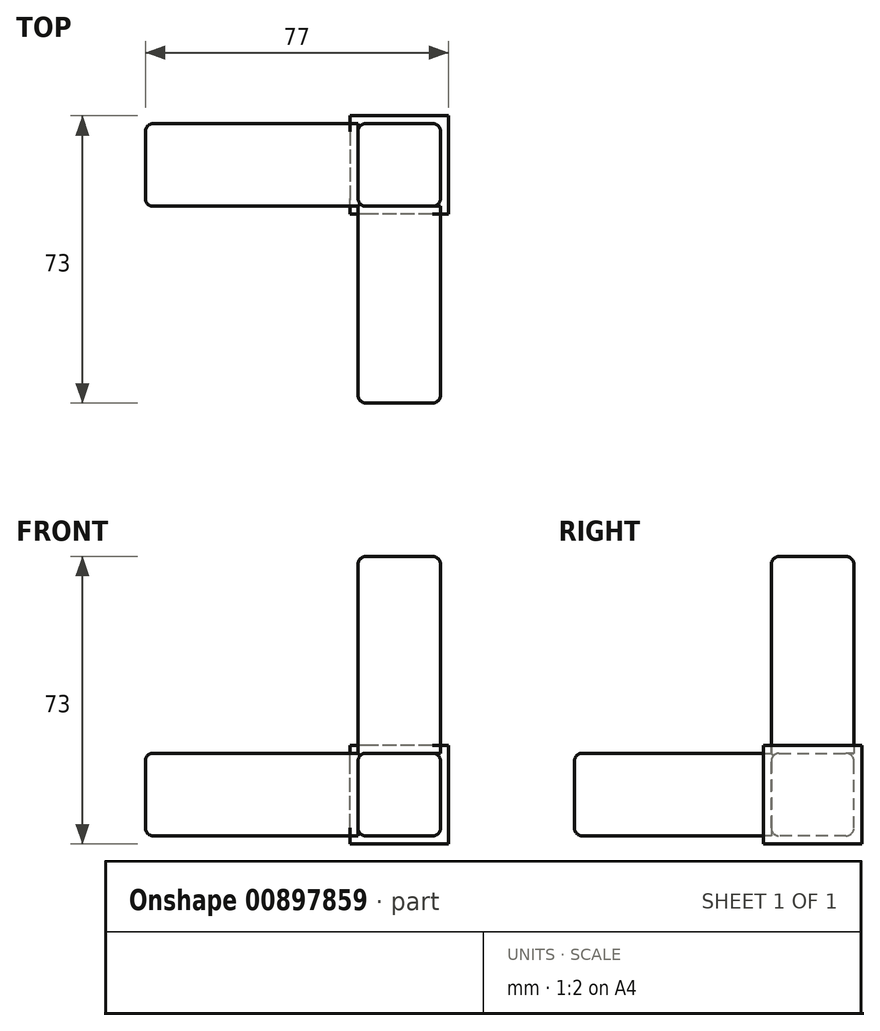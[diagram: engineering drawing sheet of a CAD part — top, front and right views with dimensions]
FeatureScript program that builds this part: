
annotation { "Feature Type Name" : "Feature", "Feature Type Description" : "" }
export const myFeature = defineFeature(function(context is Context, id is Id, definition is map)
    precondition{}
    {
        {
            var Q0;
            Q0=qCreatedBy(makeId("Front.planeOp"),FACE);
            var sketch = newSketch(context, id + "F0", { "sketchPlane" : qUnion([Q0])});
            skLineSegment(sketch, "E0.bottom", {"start": v(37.5, -10.5) * mm, "end": v(-37.5, -10.5) * mm});
            skLineSegment(sketch, "E0.top", {"start": v(16.5, 10.5) * mm, "end": v(-37.5, 10.5) * mm});
            skLineSegment(sketch, "E0.left", {"start": v(37.5, -10.5) * mm, "end": v(37.5, 10.5) * mm});
            skLineSegment(sketch, "E0.right", {"start": v(-37.5, -10.5) * mm, "end": v(-37.5, 10.5) * mm});
            skPoint(sketch, "E0.middle", {"position": v(0, 0) * mm});
            skLineSegment(sketch, "E1", {"start": v(37.5, 10.5) * mm, "end": v(37.5, 60.5) * mm});
            skLineSegment(sketch, "E2", {"start": v(37.5, 60.5) * mm, "end": v(16.5, 60.5) * mm});
            skLineSegment(sketch, "E3", {"start": v(16.5, 60.5) * mm, "end": v(16.5, 10.5) * mm});
            skLineSegment(sketch, "E4", {"start": v(16.5, 10.5) * mm, "end": v(37.5, -10.5) * mm, "construction": true});
            skLineSegment(sketch, "E5", {"start": v(37.5, 10.5) * mm, "end": v(16.5, -10.5) * mm, "construction": true});
            skLineSegment(sketch, "E6.bottom", {"start": v(39.5, -12.5) * mm, "end": v(14.5, -12.5) * mm});
            skLineSegment(sketch, "E6.top", {"start": v(39.5, 12.5) * mm, "end": v(14.5, 12.5) * mm});
            skLineSegment(sketch, "E6.left", {"start": v(39.5, -12.5) * mm, "end": v(39.5, 12.5) * mm});
            skLineSegment(sketch, "E6.right", {"start": v(14.5, -12.5) * mm, "end": v(14.5, 12.5) * mm});
            skPoint(sketch, "E6.middle", {"position": v(27, 0) * mm});
            skSolve(sketch);
        }
        {
            var Q0;
            {var subQ0=sQuery(id+"F0.wireOp",EDGE,"E2");Q0=makeQuery(id+"F0.imprint","IMPRINT",FACE,{"disambiguationData":[TD([[makeQuery(id+"F0.imprint","IMPRINT",EDGE,{"derivedFrom":subQ0}),1.0]])]});}
            var Q1;
            {var subQ0=sQuery(id+"F0.wireOp",EDGE,"E0.right");Q1=makeQuery(id+"F0.imprint","IMPRINT",FACE,{"disambiguationData":[TD([[makeQuery(id+"F0.imprint","IMPRINT",EDGE,{"derivedFrom":subQ0}),-1.0]])]});}
            var Q2;
            {var subQ1=sQuery(id+"F0.wireOp",EDGE,"E0.left");Q2=makeQuery(id+"F0.imprint","IMPRINT",FACE,{"disambiguationData":[TD([[makeQuery(id+"F0.imprint","IMPRINT",EDGE,{"derivedFrom":subQ1}),1.0]])]});}
            extrude(context, id + "F1", {"entities" : qUnion([Q0, Q1, Q2]), "depth" : 21 * mm, "offsetDistance" : 25 * mm});
        }
        {
            var Q0;
            {var subQ1=sQuery(id+"F0.wireOp",EDGE,"E0.left");Q0=makeQuery(id+"F0.imprint","IMPRINT",FACE,{"disambiguationData":[TD([[makeQuery(id+"F0.imprint","IMPRINT",EDGE,{"derivedFrom":subQ1}),-1.0]])]});}
            var Q1;
            {var subQ0=sQuery(id+"F0.wireOp",EDGE,"E3");var subQ1=sQuery(id+"F0.wireOp",EDGE,"E0.top");var subQ2=makeQuery(id+"F0.imprint","INTERSECT",VERTEX,{"derivedFrom":[subQ1,subQ0]});Q1=makeQuery(id+"F0.imprint","IMPRINT",FACE,{"disambiguationData":[TD([[makeQuery(id+"F0.imprint","IMPRINT",EDGE,{"disambiguationData":[TD([[subQ2,-1.0]])],"derivedFrom":subQ1}),-1.0]])]});}
            var Q2;
            {var subQ1=sQuery(id+"F0.wireOp",EDGE,"E0.left");Q2=makeQuery(id+"F0.imprint","IMPRINT",FACE,{"disambiguationData":[TD([[makeQuery(id+"F0.imprint","IMPRINT",EDGE,{"derivedFrom":subQ1}),1.0]])]});}
            extrude(context, id + "F2", {"entities" : qUnion([Q0, Q1, Q2]), "operationType" : NewBodyOperationType.ADD, "oppositeDirection" : true, "depth" : 2 * mm, "offsetDistance" : 25 * mm});
        }
        {
            var Q0;
            Q0=makeQuery(id+"F1.opExtrude","CAP_FACE",FACE,{"disambiguationData":[OSD([sQuery(id+"F0.wireOp",EDGE,"E0.bottom"),sQuery(id+"F0.wireOp",EDGE,"E0.top"),sQuery(id+"F0.wireOp",EDGE,"E0.left"),sQuery(id+"F0.wireOp",EDGE,"E0.right"),sQuery(id+"F0.wireOp",EDGE,"E1"),sQuery(id+"F0.wireOp",EDGE,"E2"),sQuery(id+"F0.wireOp",EDGE,"E3")])],"isStart":false});
            var sketch = newSketch(context, id + "F3", { "sketchPlane" : qUnion([Q0])});
            skPoint(sketch, "E7.0", {"position": v(14.5, 12.5) * mm});
            skPoint(sketch, "E8.0", {"position": v(39.5, 12.5) * mm});
            skPoint(sketch, "E9.0", {"position": v(39.5, -12.5) * mm});
            skPoint(sketch, "E10.0", {"position": v(14.5, -12.5) * mm});
            skLineSegment(sketch, "E11.bottom", {"start": v(14.5, 12.5) * mm, "end": v(39.5, 12.5) * mm, "construction": true});
            skLineSegment(sketch, "E11.top", {"start": v(14.5, -12.5) * mm, "end": v(39.5, -12.5) * mm, "construction": true});
            skLineSegment(sketch, "E11.left", {"start": v(14.5, 12.5) * mm, "end": v(14.5, -12.5) * mm, "construction": true});
            skLineSegment(sketch, "E11.right", {"start": v(39.5, 12.5) * mm, "end": v(39.5, -12.5) * mm});
            skLineSegment(sketch, "E12.bottom", {"start": v(16.5, 10.5) * mm, "end": v(37.5, 10.5) * mm});
            skLineSegment(sketch, "E12.top", {"start": v(16.5, -10.5) * mm, "end": v(37.5, -10.5) * mm});
            skLineSegment(sketch, "E12.left", {"start": v(16.5, 10.5) * mm, "end": v(16.5, -10.5) * mm});
            skLineSegment(sketch, "E12.right", {"start": v(37.5, 10.5) * mm, "end": v(37.5, -10.5) * mm});
            skSolve(sketch);
        }
        {
            var Q0;
            Q0=makeQuery(id+"F1.opExtrude","SWEPT_FACE",FACE,{"disambiguationData":[OSD([sQuery(id+"F0.wireOp",EDGE,"E0.left"),sQuery(id+"F0.wireOp",EDGE,"E1")])]});
            var sketch = newSketch(context, id + "F4", { "sketchPlane" : qUnion([Q0])});
            skPoint(sketch, "E13.0", {"position": v(2, 12.5) * mm});
            skPoint(sketch, "E14.0", {"position": v(2, -12.5) * mm});
            skLineSegment(sketch, "E15", {"start": v(2, 12.5) * mm, "end": v(-23, 12.5) * mm});
            skLineSegment(sketch, "E16", {"start": v(-23, 12.5) * mm, "end": v(-23, -12.5) * mm});
            skLineSegment(sketch, "E17", {"start": v(-23, -12.5) * mm, "end": v(2, -12.5) * mm});
            skLineSegment(sketch, "E18", {"start": v(2, -12.5) * mm, "end": v(2, 12.5) * mm});
            skSolve(sketch);
        }
        {
            var Q0;
            Q0=qSketchRegion(id+"F4",true);
            extrude(context, id + "F5", {"entities" : qUnion([Q0]), "operationType" : NewBodyOperationType.ADD, "depth" : 2 * mm, "offsetDistance" : 25 * mm});
        }
        {
            var Q0;
            Q0=makeQuery(id+"F1.opExtrude","SWEPT_FACE",FACE,{"disambiguationData":[OSD([sQuery(id+"F0.wireOp",EDGE,"E0.bottom")])]});
            var sketch = newSketch(context, id + "F6", { "sketchPlane" : qUnion([Q0])});
            skPoint(sketch, "E19.0", {"position": v(14.5, -2) * mm});
            skPoint(sketch, "E20.0", {"position": v(39.5, -2) * mm});
            skPoint(sketch, "E21.0", {"position": v(39.5, 23) * mm});
            skLineSegment(sketch, "E22.bottom", {"start": v(39.5, -2) * mm, "end": v(14.5, -2) * mm});
            skLineSegment(sketch, "E22.top", {"start": v(39.5, 23) * mm, "end": v(14.5, 23) * mm});
            skLineSegment(sketch, "E22.left", {"start": v(39.5, -2) * mm, "end": v(39.5, 23) * mm});
            skLineSegment(sketch, "E22.right", {"start": v(14.5, -2) * mm, "end": v(14.5, 23) * mm});
            skSolve(sketch);
        }
        {
            var Q0;
            Q0=qSketchRegion(id+"F6",true);
            extrude(context, id + "F7", {"entities" : qUnion([Q0]), "operationType" : NewBodyOperationType.ADD, "depth" : 2 * mm, "offsetDistance" : 25 * mm});
        }
        {
            var Q0;
            Q0=makeQuery(id+"F3.imprint","IMPRINT",FACE,{"disambiguationData":[TD([[makeQuery(id+"F3.imprint","IMPRINT",EDGE,{"derivedFrom":sQuery(id+"F3.wireOp",EDGE,"E12.bottom")}),-1.0]])]});
            extrude(context, id + "F8", {"entities" : qUnion([Q0]), "operationType" : NewBodyOperationType.ADD, "depth" : 50 * mm, "offsetDistance" : 25 * mm});
        }
        {
            var Q0;
            Q0 = qSketchRegion(id + "F4", true);
            extrude(context, id + "F9", {"entities" : qUnion([Q0]), "operationType" : NewBodyOperationType.ADD, "depth" : 2 * mm, "offsetDistance" : 25 * mm});
        }
        {
            var Q0;
            Q0 = qSketchRegion(id + "F6", true);
            extrude(context, id + "F10", {"entities" : qUnion([Q0]), "operationType" : NewBodyOperationType.ADD, "depth" : 2 * mm, "offsetDistance" : 25 * mm});
        }
        {
            var Q0;
            Q0=makeQuery(id+"F8.opExtrude","SWEPT_EDGE",EDGE,{"disambiguationData":[OSD([sQuery(id+"F0.wireOp",EDGE,"E0.top"),sQuery(id+"F0.wireOp",EDGE,"E3"),sQuery(id+"F3.wireOp",EDGE,"E12.bottom"),sQuery(id+"F3.wireOp",EDGE,"E12.left")])]});
            var Q1;
            {var subQ0=sQuery(id+"F3.wireOp",EDGE,"E12.bottom");var subQ1=sQuery(id+"F3.wireOp",EDGE,"E12.right");Q1=makeQuery(id+"F8.boolean.opBoolean","SPLIT",EDGE,{"disambiguationData":[topologyDisambiguationEdgeConnected([makeQuery(id+"F8.opExtrude","SWEPT_FACE",FACE,{"disambiguationData":[OSD([subQ1])]})])],"derivedFrom":makeQuery(id+"F8.opExtrude","SWEPT_EDGE",EDGE,{"disambiguationData":[OSD([sQuery(id+"F0.wireOp",EDGE,"E0.left"),sQuery(id+"F0.wireOp",EDGE,"E1"),subQ0,subQ1])]})});}
            var Q2;
            {var subQ0=sQuery(id+"F3.wireOp",EDGE,"E12.top");var subQ1=sQuery(id+"F3.wireOp",EDGE,"E12.left");Q2=makeQuery(id+"F8.boolean.opBoolean","SPLIT",EDGE,{"disambiguationData":[topologyDisambiguationEdgeConnected([makeQuery(id+"F8.opExtrude","SWEPT_FACE",FACE,{"disambiguationData":[OSD([subQ0])]})])],"derivedFrom":makeQuery(id+"F8.opExtrude","SWEPT_EDGE",EDGE,{"disambiguationData":[OSD([sQuery(id+"F0.wireOp",EDGE,"E0.bottom"),subQ0,subQ1])]})});}
            var Q3;
            Q3=makeQuery(id+"F8.opExtrude","SWEPT_EDGE",EDGE,{"disambiguationData":[OSD([sQuery(id+"F3.wireOp",EDGE,"E12.top"),sQuery(id+"F3.wireOp",EDGE,"E12.right")])]});
            var Q4;
            Q4=makeQuery(id+"F8.opExtrude","CAP_EDGE",EDGE,{"disambiguationData":[OSD([sQuery(id+"F3.wireOp",EDGE,"E12.top")])],"isStart":false});
            var Q5;
            Q5=makeQuery(id+"F8.opExtrude","CAP_EDGE",EDGE,{"disambiguationData":[OSD([sQuery(id+"F3.wireOp",EDGE,"E12.left")])],"isStart":false});
            var Q6;
            Q6=makeQuery(id+"F8.opExtrude","CAP_EDGE",EDGE,{"disambiguationData":[OSD([sQuery(id+"F3.wireOp",EDGE,"E12.bottom")])],"isStart":false});
            var Q7;
            Q7=makeQuery(id+"F8.opExtrude","CAP_EDGE",EDGE,{"disambiguationData":[OSD([sQuery(id+"F3.wireOp",EDGE,"E12.right")])],"isStart":false});
            fillet(context, id + "F11", {"entities" : qUnion([Q0, Q1, Q2, Q3, Q4, Q5, Q6, Q7]), "radius" : 2 * mm, "tangentPropagation" : true, "allowEdgeOverflow" : false});
        }
        {
            var Q0;
            Q0=makeQuery(id+"F1.opExtrude","CAP_EDGE",EDGE,{"disambiguationData":[OSD([sQuery(id+"F0.wireOp",EDGE,"E0.top")])],"isStart":false});
            var Q1;
            {var subQ0=sQuery(id+"F0.wireOp",EDGE,"E0.top");Q1=makeQuery(id+"F2.boolean.opBoolean","SPLIT",EDGE,{"disambiguationData":[topologyDisambiguationEdgeConnected([makeQuery(id+"F1.opExtrude","CAP_FACE",FACE,{"disambiguationData":[OSD([sQuery(id+"F0.wireOp",EDGE,"E0.bottom"),subQ0,sQuery(id+"F0.wireOp",EDGE,"E0.left"),sQuery(id+"F0.wireOp",EDGE,"E0.right"),sQuery(id+"F0.wireOp",EDGE,"E1"),sQuery(id+"F0.wireOp",EDGE,"E2"),sQuery(id+"F0.wireOp",EDGE,"E3")])],"isStart":true})])],"derivedFrom":makeQuery(id+"F1.opExtrude","CAP_EDGE",EDGE,{"disambiguationData":[OSD([subQ0])],"isStart":true})});}
            var Q2;
            {var subQ0=sQuery(id+"F0.wireOp",EDGE,"E0.bottom");Q2=makeQuery(id+"F2.boolean.opBoolean","SPLIT",EDGE,{"disambiguationData":[topologyDisambiguationEdgeConnected([makeQuery(id+"F1.opExtrude","CAP_FACE",FACE,{"disambiguationData":[OSD([subQ0,sQuery(id+"F0.wireOp",EDGE,"E0.top"),sQuery(id+"F0.wireOp",EDGE,"E0.left"),sQuery(id+"F0.wireOp",EDGE,"E0.right"),sQuery(id+"F0.wireOp",EDGE,"E1"),sQuery(id+"F0.wireOp",EDGE,"E2"),sQuery(id+"F0.wireOp",EDGE,"E3")])],"isStart":true})])],"derivedFrom":makeQuery(id+"F1.opExtrude","CAP_EDGE",EDGE,{"disambiguationData":[OSD([subQ0])],"isStart":true})});}
            var Q3;
            {var subQ0=sQuery(id+"F0.wireOp",EDGE,"E0.bottom");Q3=makeQuery(id+"F7.boolean.opBoolean","SPLIT",EDGE,{"disambiguationData":[topologyDisambiguationEdgeConnected([makeQuery(id+"F1.opExtrude","SWEPT_FACE",FACE,{"disambiguationData":[OSD([subQ0])]})])],"derivedFrom":makeQuery(id+"F1.opExtrude","CAP_EDGE",EDGE,{"disambiguationData":[OSD([subQ0])],"isStart":false})});}
            var Q4;
            Q4=makeQuery(id+"F1.opExtrude","CAP_EDGE",EDGE,{"disambiguationData":[OSD([sQuery(id+"F0.wireOp",EDGE,"E0.right")])],"isStart":false});
            var Q5;
            Q5=makeQuery(id+"F1.opExtrude","SWEPT_EDGE",EDGE,{"disambiguationData":[OSD([sQuery(id+"F0.wireOp",EDGE,"E0.top"),sQuery(id+"F0.wireOp",EDGE,"E0.right")])]});
            var Q6;
            Q6=makeQuery(id+"F1.opExtrude","CAP_EDGE",EDGE,{"disambiguationData":[OSD([sQuery(id+"F0.wireOp",EDGE,"E0.right")])],"isStart":true});
            var Q7;
            Q7=makeQuery(id+"F1.opExtrude","SWEPT_EDGE",EDGE,{"disambiguationData":[OSD([sQuery(id+"F0.wireOp",EDGE,"E0.bottom"),sQuery(id+"F0.wireOp",EDGE,"E0.right")])]});
            fillet(context, id + "F12", {"entities" : qUnion([Q0, Q1, Q2, Q3, Q4, Q5, Q6, Q7]), "radius" : 2 * mm, "tangentPropagation" : true, "allowEdgeOverflow" : false});
        }
        {
            var Q0;
            {var subQ0=sQuery(id+"F0.wireOp",EDGE,"E3");Q0=makeQuery(id+"F2.boolean.opBoolean","SPLIT",EDGE,{"disambiguationData":[topologyDisambiguationEdgeConnected([makeQuery(id+"F1.opExtrude","CAP_FACE",FACE,{"disambiguationData":[OSD([sQuery(id+"F0.wireOp",EDGE,"E0.bottom"),sQuery(id+"F0.wireOp",EDGE,"E0.top"),sQuery(id+"F0.wireOp",EDGE,"E0.left"),sQuery(id+"F0.wireOp",EDGE,"E0.right"),sQuery(id+"F0.wireOp",EDGE,"E1"),sQuery(id+"F0.wireOp",EDGE,"E2"),subQ0])],"isStart":true})])],"derivedFrom":makeQuery(id+"F1.opExtrude","CAP_EDGE",EDGE,{"disambiguationData":[OSD([subQ0])],"isStart":true})});}
            var Q1;
            Q1=makeQuery(id+"F1.opExtrude","CAP_EDGE",EDGE,{"disambiguationData":[OSD([sQuery(id+"F0.wireOp",EDGE,"E3")])],"isStart":false});
            var Q2;
            {var subQ0=sQuery(id+"F0.wireOp",EDGE,"E1");var subQ1=sQuery(id+"F0.wireOp",EDGE,"E0.left");Q2=makeQuery(id+"F2.boolean.opBoolean","SPLIT",EDGE,{"disambiguationData":[topologyDisambiguationEdgeConnected([makeQuery(id+"F1.opExtrude","CAP_FACE",FACE,{"disambiguationData":[OSD([sQuery(id+"F0.wireOp",EDGE,"E0.bottom"),sQuery(id+"F0.wireOp",EDGE,"E0.top"),subQ1,sQuery(id+"F0.wireOp",EDGE,"E0.right"),subQ0,sQuery(id+"F0.wireOp",EDGE,"E2"),sQuery(id+"F0.wireOp",EDGE,"E3")])],"isStart":true})])],"derivedFrom":makeQuery(id+"F1.opExtrude","CAP_EDGE",EDGE,{"disambiguationData":[OSD([subQ1,subQ0])],"isStart":true})});}
            var Q3;
            {var subQ0=sQuery(id+"F0.wireOp",EDGE,"E1");var subQ1=sQuery(id+"F0.wireOp",EDGE,"E0.left");Q3=makeQuery(id+"F5.boolean.opBoolean","SPLIT",EDGE,{"disambiguationData":[topologyDisambiguationEdgeConnected([makeQuery(id+"F1.opExtrude","SWEPT_FACE",FACE,{"disambiguationData":[OSD([subQ1,subQ0])]})])],"derivedFrom":makeQuery(id+"F1.opExtrude","CAP_EDGE",EDGE,{"disambiguationData":[OSD([subQ1,subQ0])],"isStart":false})});}
            var Q4;
            Q4=makeQuery(id+"F1.opExtrude","CAP_EDGE",EDGE,{"disambiguationData":[OSD([sQuery(id+"F0.wireOp",EDGE,"E2")])],"isStart":false});
            var Q5;
            Q5=makeQuery(id+"F1.opExtrude","SWEPT_EDGE",EDGE,{"disambiguationData":[OSD([sQuery(id+"F0.wireOp",EDGE,"E1"),sQuery(id+"F0.wireOp",EDGE,"E2")])]});
            var Q6;
            Q6=makeQuery(id+"F1.opExtrude","SWEPT_EDGE",EDGE,{"disambiguationData":[OSD([sQuery(id+"F0.wireOp",EDGE,"E2"),sQuery(id+"F0.wireOp",EDGE,"E3")])]});
            var Q7;
            Q7=makeQuery(id+"F1.opExtrude","CAP_EDGE",EDGE,{"disambiguationData":[OSD([sQuery(id+"F0.wireOp",EDGE,"E2")])],"isStart":true});
            fillet(context, id + "F13", {"entities" : qUnion([Q0, Q1, Q2, Q3, Q4, Q5, Q6, Q7]), "radius" : 2 * mm, "tangentPropagation" : true, "allowEdgeOverflow" : false});
        }
    });
